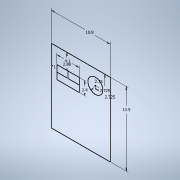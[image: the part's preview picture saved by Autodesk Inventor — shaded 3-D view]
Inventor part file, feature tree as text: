
AUTODESK INVENTOR PART (.ipt)
format: ipt  version: 2022 (Build 260153070, 153G)  size: 117,248 bytes
history: native  units: mm
features: extrude x2, sketch x1
ambient origin geometry x8: Origin, YZ Plane, XZ Plane, XY Plane, X Axis, Y Axis, Z Axis, Center Point
bodies: Solid1 (feature_tree)
feature tree (3):
  sketch  "Sketch1"  dims[d0=10.8mm d1=13.5mm d2=2.725mm d3=2.725mm d4=2.75mm d5=4.1mm d6=2.4mm d7=1.0mm d8=2.88mm d9=1.65mm d10=0.0mm d11=2.75mm d12=0.0mm]
  extrude  "Extrusion1"  Depth=13.5mm
  extrude  "Extrusion2"  Depth=2.75mm
